# Revit family: LEXIEK032# - Lexie
name_source: partatom
category: Furniture
revit_build: Autodesk Revit 2014 (Build: 20131024_2115(x64)
units: mm (PartAtom-declared; Revit-internal decimal feet)

## types (6) — shared parameters
CatURL = http://www.knightsbridge-furniture.co.uk
Dim 2 (D) = 790 mm  [stored 2.59186 ft]
Dim 3 (H) = 830 mm  [stored 2.7231 ft]
Finish & Fabrics = http://www.knightsbridge-furniture.co.uk
Manufacturer = Knightsbridge Furniture Productions Ltd.
Product Range = Tubs Clubs and Upholstered Seating
Type Comments = Ergonomically styled to ensure a comfortable sit over long periods
URL = http://www.knightsbridge-furniture.co.uk

## per-type parameters (varying)
| type | CatRef | Description | Dim 1 (W) | Model |
| LEXIEK0321 - Lexie Armchair-870w x 790d x 830mm High | LEXIEK0321 | Lexie Armchair | 870 mm  [stored 2.85433 ft] | Armchair |
| LEXIEK0322 - Lexie 2 seater Settee-1560w x 790d x 830mm High | LEXIEK0322 | Lexie 2 seater Settee | 1560 mm  [stored 5.11811 ft] | Two seater Settee |
| LEXIEK0323 - Lexie 3 seater Settee-1845w x 790d x 830mm High | LEXIEK0323 | Lexie 3 seater Settee | 1845 mm | Three seater Settee |
| LEXIEK0321X - Lexie Armchair Extreme-870w x 790d x 830mm High | LEXIEK0321X | Lexie Armchair Extreme | 870 mm  [stored 2.85433 ft] | Armchair |
| LEXIEK0322X - Lexie 2 seater Settee Extreme-1560w x 790d x 830mm High | LEXIEK0322X | Lexie 2 seater Settee Extreme | 1560 mm  [stored 5.11811 ft] | Two seater Settee |
| LEXIEK0323X - Lexie 3 seater Settee Extreme-1845w x 790d x 830mm High | LEXIEK0323X | Lexie 3 seater Settee Extreme | 1845 mm | Three seater Settee |

note: [stored X ft] marks values corroborated as IEEE doubles in the binary element streams (Revit-internal decimal feet)

## geometry (parser evidence)
native form markers: Sweep x5
no freeform markers — native parametric forms only
